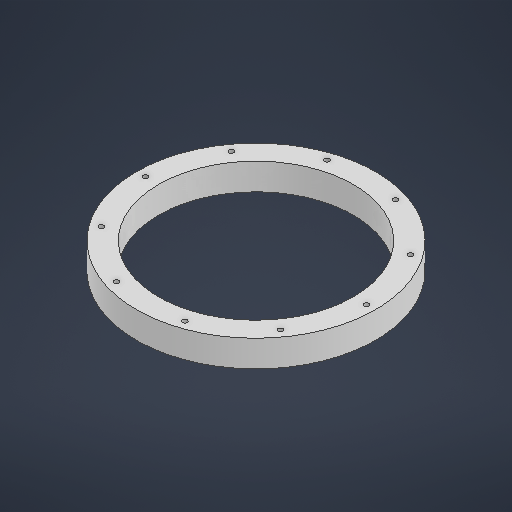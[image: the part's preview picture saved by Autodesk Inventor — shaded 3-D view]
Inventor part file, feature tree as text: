
AUTODESK INVENTOR PART (.ipt)
format: ipt  version: 2025 (Build 290162000, 162)  size: 244,224 bytes
history: native  units: in
note: dims shown in document units (in); Inventor stores cm internally (conversion verified against a paired STEP export)
features: sketch x9, extrude x6, hole x1
ambient origin geometry x8: Origin, YZ Plane, XZ Plane, XY Plane, X Axis, Y Axis, Z Axis, Center Point
bodies: Solid1 (feature_tree)
feature tree (16):
  extrude  "Extrusion1"  Depth=8.6614in
  hole  "Hole1"  [1 undecoded]
  extrude  "Extrusion7"  Depth=3.937in TaperAngle=360.0deg
  extrude  "Extrusion8"  Depth=0.3937in
  extrude  "Extrusion9"  Depth=0.3937in TaperAngle=0.0deg
  extrude  "Extrusion10"  Depth=5.1181in
  extrude  "Extrusion11"  Depth=5.9055in
  sketch  "Sketch1"  dims[d0=10.6299in d1=8.6614in]
  sketch  "Sketch3"  dims[d9=0.1575in d10=3.937in d12=360.0deg]
  sketch  "Sketch Circular Pattern1"  dims[d2=1.1811in d3=0.0in d8=9.8425in]
  sketch  "Sketch8"  dims[d37=0.3937in d38=0.0in d39=0.1969in d40=0.0in]
  sketch  "Sketch9"  dims[d41=8.6614in d42=5.1181in]
  sketch  "Sketch10"  dims[d43=0.0984in d44=0.0in d45=5.9055in]
  sketch  "Sketch11"  dims[d46=6.0236in]
  sketch  "Sketch12"  dims[d47=0.0197in d48=0.0in d49=6.6929in d55=0.2165in d56=2.3622in d58=360.0deg d60=0.0197in d61=0.0in d24=0.0197in d25=0.0344in d26=0.0197in d27=0.0344in d30=0.0197in d31=0.0344in d32=0.0197in d33=0.0344in d34=0.0197in d35=0.0344in]
  sketch  "Sketch Circular Pattern3"  dims[d14=0.2165in d15=0.3937in d16=0.1575in d17=0.0787in d18=90.0deg d19=0.315in d20=0.8108in d36=4.9213in]
note: 1 required parameter value undecoded (feature->parameter linkage not recoverable at this tier; creation-order binding heuristic only, values carry confidence <= 0.55)
